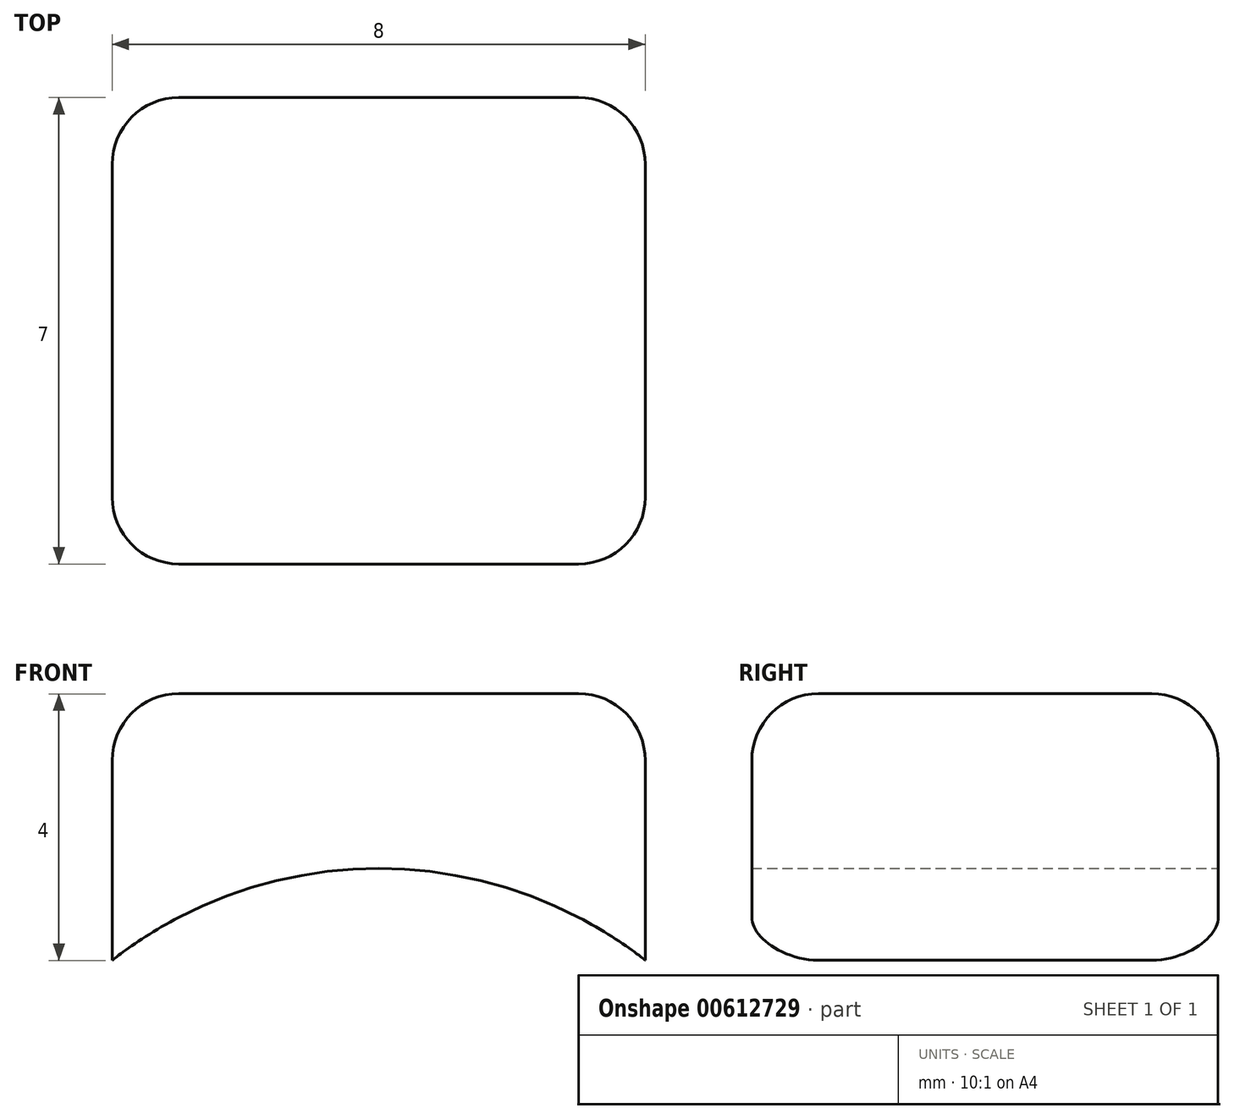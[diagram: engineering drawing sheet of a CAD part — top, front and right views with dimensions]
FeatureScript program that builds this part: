
annotation { "Feature Type Name" : "Feature", "Feature Type Description" : "" }
export const myFeature = defineFeature(function(context is Context, id is Id, definition is map)
    precondition{}
    {
        {
            var Q0;
            Q0=qCreatedBy(makeId("Front.planeOp"),FACE);
            var sketch = newSketch(context, id + "F0", { "sketchPlane" : qUnion([Q0])});
            skLineSegment(sketch, "E0.bottom", {"start": v(-4, 9.12) * mm, "end": v(4, 9.12) * mm});
            skLineSegment(sketch, "E0.left", {"start": v(-4, 9.12) * mm, "end": v(-4, 5.12) * mm});
            skLineSegment(sketch, "E0.right", {"start": v(4, 9.12) * mm, "end": v(4, 5.12) * mm});
            skArc(sketch, "E1", {"start": v(4, 5.12) * mm, "mid": v(0, 6.5) * mm, "end": v(-4, 5.12) * mm});
            skSolve(sketch);
        }
        {
            var Q0;
            Q0=qSketchRegion(id+"F0",true);
            extrude(context, id + "F1", {"entities" : qUnion([Q0]), "depth" : 7 * mm, "offsetDistance" : 25 * mm});
        }
        {
            var Q0;
            Q0=makeQuery(id+"F1.opExtrude","CAP_EDGE",EDGE,{"disambiguationData":[OSD([sQuery(id+"F0.wireOp",EDGE,"E0.left")])],"isStart":false});
            var Q1;
            Q1=makeQuery(id+"F1.opExtrude","CAP_EDGE",EDGE,{"disambiguationData":[OSD([sQuery(id+"F0.wireOp",EDGE,"E0.right")])],"isStart":false});
            var Q2;
            Q2=makeQuery(id+"F1.opExtrude","CAP_EDGE",EDGE,{"disambiguationData":[OSD([sQuery(id+"F0.wireOp",EDGE,"E0.right")])],"isStart":true});
            var Q3;
            Q3=makeQuery(id+"F1.opExtrude","CAP_EDGE",EDGE,{"disambiguationData":[OSD([sQuery(id+"F0.wireOp",EDGE,"E0.left")])],"isStart":true});
            var Q4;
            Q4=makeQuery(id+"F1.opExtrude","SWEPT_FACE",FACE,{"disambiguationData":[OSD([sQuery(id+"F0.wireOp",EDGE,"E0.bottom")])]});
            fillet(context, id + "F2", {"entities" : qUnion([Q0, Q1, Q2, Q3, Q4]), "radius" : 1 * mm, "tangentPropagation" : true, "allowEdgeOverflow" : false});
        }
    });
